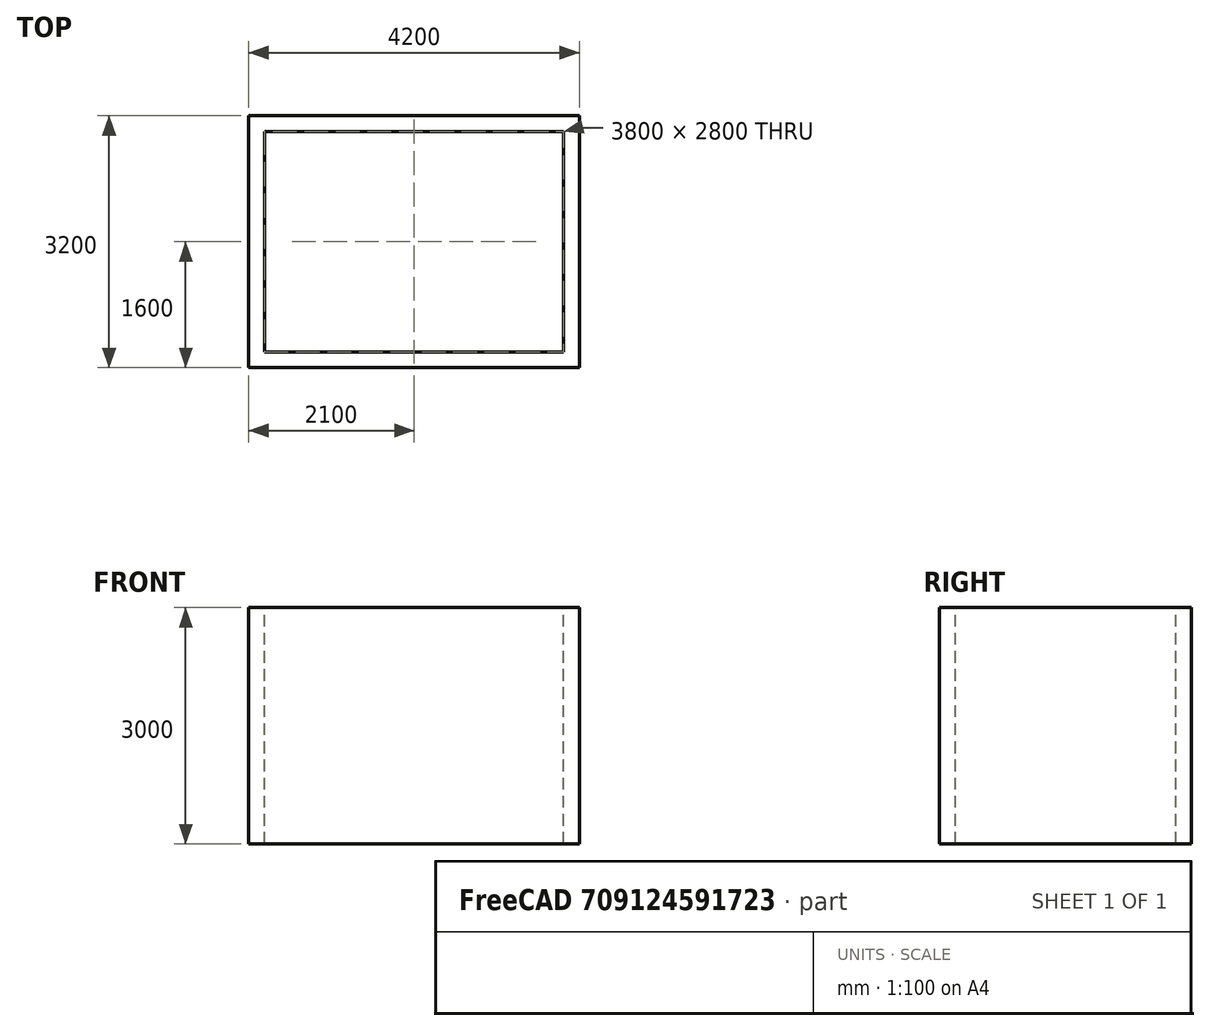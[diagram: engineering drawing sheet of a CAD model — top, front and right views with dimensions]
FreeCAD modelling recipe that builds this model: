
FCSTD DOCUMENT  (FreeCAD 0.20R29603 (Git))
Label: 20230526-freecad-arch-working-plane
License: All rights reserved
LicenseURL: http://en.wikipedia.org/wiki/All_rights_reserved
objects: Part::Part2DObjectPython×1, Part::FeaturePython×1
note: 2 computed .brp shape members not serialized (recipe doc carries the construction recipe); baked Part::Feature solids carry a one-line shape summary decoded from their .brp

FEATURE [Part::Part2DObjectPython] Rectangle  # Draft 2D object (typed FeaturePython)
  Area = 0
  ChamferSize = 0
  Columns = 1
  FilletRadius = 0
  Height = 3000
  Length = 4000
  MakeFace = false
  Placement = pos=(-33.3139,-34.186,0) rot=(0,0,1;0rad)
  Rows = 1
FEATURE [Part::FeaturePython] Wall  # Arch/BIM 166 (typed FeaturePython)
  Align = 2
  Area = 42000000
  Base = -> Rectangle
  BlockHeight = 0
  BlockLength = 0
  CountBroken = 0
  CountEntire = 0
  Face = 0
  Height = 3000
  HorizontalArea = 2.8e+06
  IfcData = attributes={"GlobalId": {"name": "GlobalId", "type": "IfcGloballyUniqueId", "is_enum": false, "enum_values": []}, "Description": {"... (+533 chars omitted),+1 more (map truncated)
  IfcType = 166
  Joint = 0
  Length = 14000
  MakeBlocks = false
  MoveBase = false
  MoveWithHost = false
  Normal = (0,0,0)
  OffsetFirst = 0
  OffsetSecond = 0
  PerimeterLength = 14800
  PredefinedType = 0
  VerticalArea = 84000000
  Width = 200
